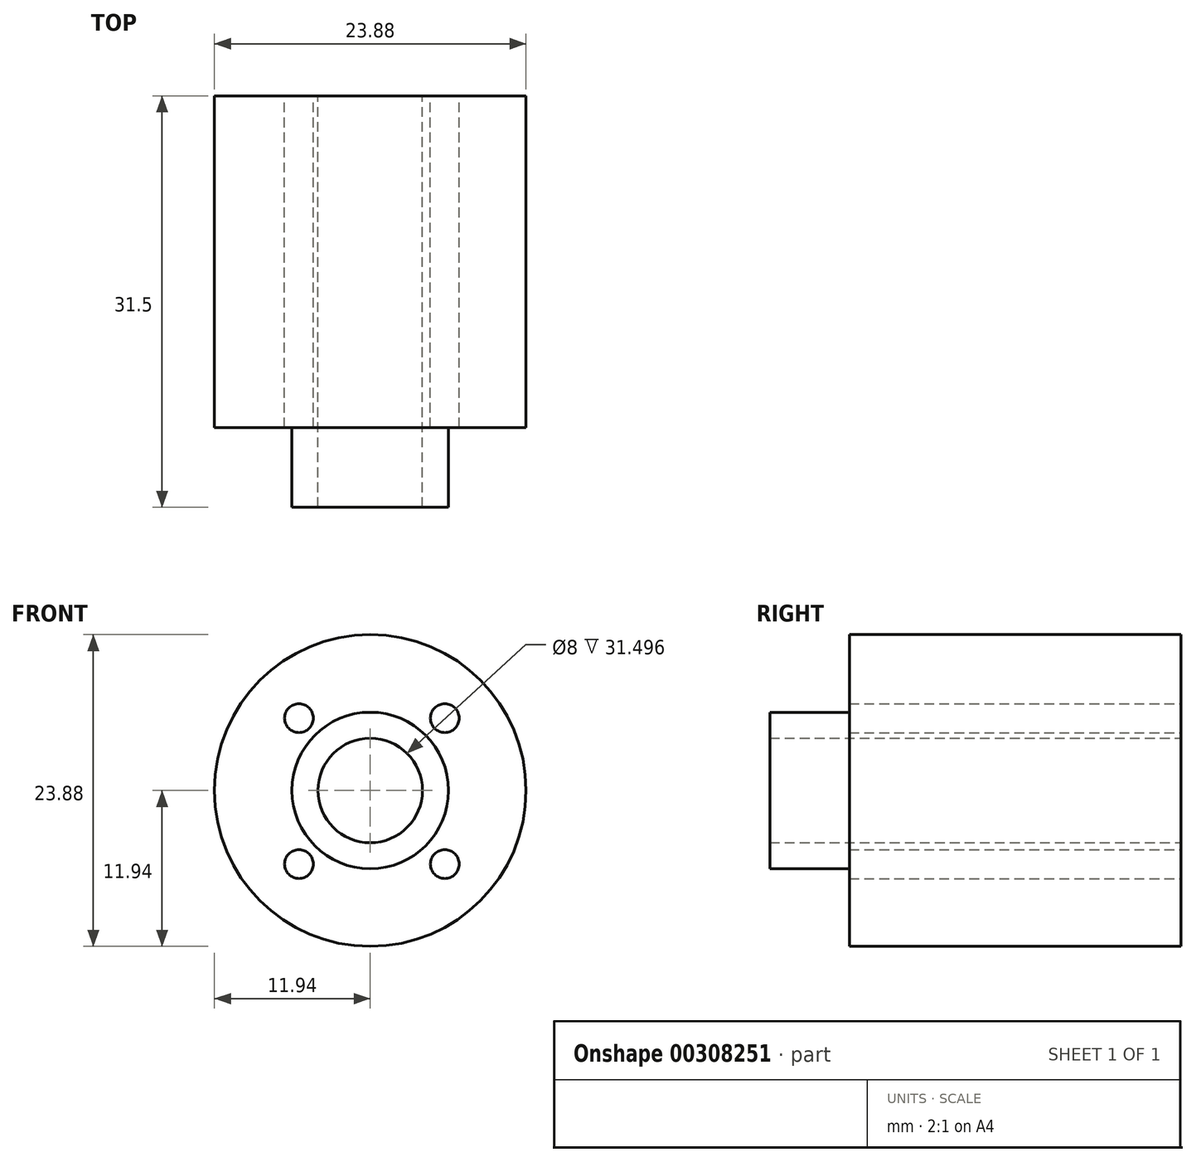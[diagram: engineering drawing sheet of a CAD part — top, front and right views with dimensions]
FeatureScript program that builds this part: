
annotation { "Feature Type Name" : "Feature", "Feature Type Description" : "" }
export const myFeature = defineFeature(function(context is Context, id is Id, definition is map)
    precondition{}
    {
        {
            var Q0;
            Q0=qCreatedBy(makeId("Front.planeOp"),FACE);
            var sketch = newSketch(context, id + "F0", { "sketchPlane" : qUnion([Q0])});
            skCircle(sketch, "E0", {"center": v(0, 0) * mm, "radius": 11.94 * mm});
            skCircle(sketch, "E1", {"center": v(0, 0) * mm, "radius": 6 * mm});
            skCircle(sketch, "E2", {"center": v(0, 0) * mm, "radius": 4 * mm});
            skCircle(sketch, "E3", {"center": v(-5.46, 5.54) * mm, "radius": 1.1 * mm});
            skCircle(sketch, "E4", {"center": v(-5.46, -5.64) * mm, "radius": 1.1 * mm});
            skCircle(sketch, "E5", {"center": v(5.71, -5.64) * mm, "radius": 1.1 * mm});
            skCircle(sketch, "E6", {"center": v(5.71, 5.54) * mm, "radius": 1.1 * mm});
            skPoint(sketch, "E7", {"position": v(-11.94, 0) * mm});
            skPoint(sketch, "E8", {"position": v(11.94, 0) * mm});
            skSolve(sketch);
        }
        {
            var Q0;
            Q0=makeQuery(id+"F0.imprint","IMPRINT",FACE,{"disambiguationData":[TD([[makeQuery(id+"F0.imprint","IMPRINT",EDGE,{"derivedFrom":sQuery(id+"F0.wireOp",EDGE,"E0")}),1.0]])]});
            extrude(context, id + "F1", {"entities" : qUnion([Q0]), "depth" : 25.4 * mm});
        }
        {
            var Q0;
            Q0=makeQuery(id+"F0.imprint","IMPRINT",FACE,{"disambiguationData":[TD([[makeQuery(id+"F0.imprint","IMPRINT",EDGE,{"derivedFrom":sQuery(id+"F0.wireOp",EDGE,"E1")}),1.0]])]});
            extrude(context, id + "F2", {"entities" : qUnion([Q0]), "operationType" : NewBodyOperationType.ADD, "depth" : 31.5 * mm});
        }
    });
